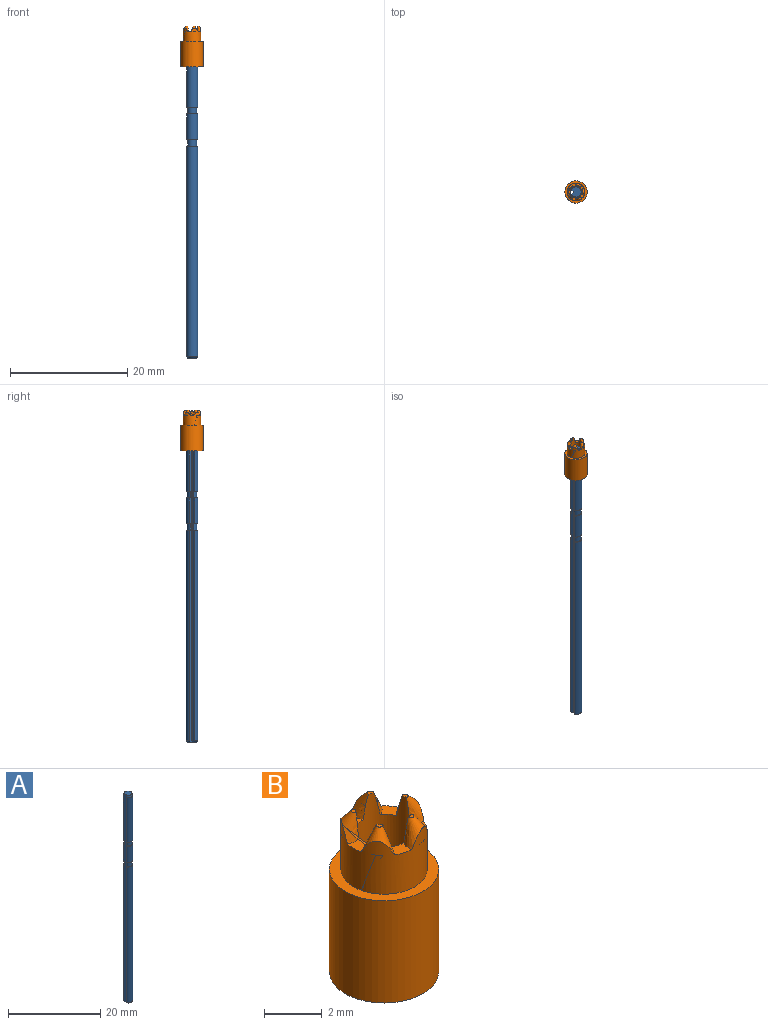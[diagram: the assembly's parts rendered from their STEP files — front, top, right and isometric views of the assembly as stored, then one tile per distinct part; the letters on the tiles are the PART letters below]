
ASSEMBLY  parts=2 mates=1
PART A: 16 faces, bbox 1.9x2x55 mm
  f0: cylinder r=1mm len=4.4mm, axis (0,0,-1), area 23.3mm2, adj f3,f5,f11,f15
  f1: cylinder r=1mm len=35.95mm, axis (0,0,-1), area 190mm2, adj f3,f5,f8,f12
  f2: cylinder r=0.1mm len=55mm, axis (0,0,-1), area 8.6mm2, adj f3,f5,f6,f7
  f3: plane 55.01x0.42mm, normal (-0.71,0.71,0), area 31.2mm2, adj f0,f1,f2,f4,f6,f7,f8,f9
  f4: cylinder r=1mm len=11.75mm, axis (0,0,-1), area 62.1mm2, adj f3,f5,f9,f14
  f5: plane 55.01x0.42mm, normal (-0.71,-0.71,0), area 31.2mm2, adj f0,f1,f2,f4,f6,f7,f8,f9
  f6: plane 1.73x1.65mm, normal (0,0,1), area 2.2mm2, adj f2,f3,f5,f9
  f7: plane 1.6x1.53mm, normal (0,0,-1), area 1.9mm2, adj f2,f3,f5,f8
  f8: cone r=1mm half-angle=45deg, axis (0,0,1), area 1.4mm2, adj f1,f3,f5,f7
  f9: cone r=0.87mm half-angle=15deg, axis (0,0,-1), area 2.6mm2, adj f3,f4,f5,f6
  f10: cylinder r=0.8mm len=1.6mm, axis (0,0,-1), area 4.8mm2, adj f3,f5,f11,f12
  f11: plane 2x1.88mm, normal (0,0,-1), area 1mm2, adj f0,f3,f5,f10
  f12: plane 2x1.88mm, normal (0,0,1), area 1mm2, adj f1,f3,f5,f10
  f13: cylinder r=0.8mm len=1.6mm, axis (0,0,-1), area 4.8mm2, adj f3,f5,f14,f15
  f14: plane 2x1.88mm, normal (0,0,-1), area 1mm2, adj f3,f4,f5,f13
  f15: plane 2x1.88mm, normal (0,0,1), area 1mm2, adj f0,f3,f5,f13
PART B: 30 faces, bbox 3.9x3.9x7.1 mm
  f0: plane 0.39x0.02mm, normal (0.34,0,-0.94), area 0mm2, adj f4,f5
  f1: cone r=0.6mm half-angle=24.8deg, axis (0.34,0,-0.94), area 1mm2, adj f2,f3,f4,f6,f26
  f2: plane 0.34x0.27mm, normal (0,0,1), area 0mm2, adj f1,f3
  f3: cylinder r=1mm len=6.95mm, axis (0,0,-1), area 39.8mm2, adj f1,f2,f6,f7,f9,f11,f12,f14
  f4: cylinder r=1.5mm len=3mm, axis (0,0,-1), area 17.9mm2, adj f0,f1,f5,f6,f8,f9,f10,f11
  f5: plane 0.38x0.01mm, normal (0,0,1), area 0mm2, adj f0,f4
  f6: plane 0.83x0.8mm, normal (0,0,1), area 0.3mm2, adj f1,f3,f4,f9
  f7: plane 0.34x0.3mm, normal (0,0,1), area 0mm2, adj f3,f9
  f8: plane 0.37x0.13mm, normal (0.11,0.33,-0.94), area 0mm2, adj f4,f10
  f9: cone r=0.6mm half-angle=24.8deg, axis (0.11,0.33,-0.94), area 1mm2, adj f3,f4,f6,f7,f11
  f10: plane 0.37x0.12mm, normal (0,0,1), area 0mm2, adj f4,f8
  f11: plane 0.78x0.7mm, normal (0,0,1), area 0.3mm2, adj f3,f4,f9,f14
  f12: plane 0.34x0.32mm, normal (0,0,1), area 0mm2, adj f3,f14
  f13: plane 0.32x0.23mm, normal (-0.28,0.2,-0.94), area 0mm2, adj f4,f15
  f14: cone r=0.6mm half-angle=24.8deg, axis (-0.28,0.2,-0.94), area 1mm2, adj f3,f4,f11,f12,f16
  f15: plane 0.31x0.23mm, normal (0,0,1), area 0mm2, adj f4,f13
  f16: plane 0.71x0.57mm, normal (0,0,1), area 0.3mm2, adj f3,f4,f14,f19
  f17: plane 0.34x0.32mm, normal (0,0,1), area 0mm2, adj f3,f19
  f18: plane 0.32x0.23mm, normal (-0.28,-0.2,-0.94), area 0mm2, adj f4,f20
  f19: cone r=0.6mm half-angle=24.8deg, axis (-0.28,-0.2,-0.94), area 1mm2, adj f3,f4,f16,f17,f21
  f20: plane 0.31x0.23mm, normal (0,0,1), area 0mm2, adj f4,f18
  f21: plane 0.78x0.7mm, normal (0,0,1), area 0.3mm2, adj f3,f4,f19,f23
  f22: plane 0.37x0.13mm, normal (0.11,-0.33,-0.94), area 0mm2, adj f4,f25
  f23: cone r=0.6mm half-angle=24.8deg, axis (0.11,-0.33,-0.94), area 1mm2, adj f3,f4,f21,f24,f26
  f24: plane 0.34x0.3mm, normal (0,0,1), area 0mm2, adj f3,f23
  f25: plane 0.37x0.12mm, normal (0,0,1), area 0mm2, adj f4,f22
  f26: plane 0.83x0.8mm, normal (0,0,1), area 0.3mm2, adj f1,f3,f4,f23
  f27: cylinder r=1.9mm len=4.35mm, axis (0,0,1), area 51.9mm2, adj f28,f29
  f28: plane 3.8x3.8mm, normal (0,0,-1), area 8.2mm2, adj f3,f27
  f29: plane 3.8x3.8mm, normal (0,0,1), area 4.3mm2, adj f4,f27
PLACE A t=(0,0,-54.05)mm
PLACE B at identity fixed
MATE fastened A.f0 <-> B.f3  axis (0,0,1) through (0,0,0.95)mm
